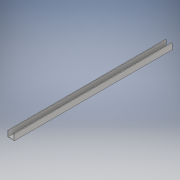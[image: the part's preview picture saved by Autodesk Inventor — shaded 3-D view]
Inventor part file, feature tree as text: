
AUTODESK INVENTOR PART (.ipt)
format: ipt  version: 2017 (Build 210142000, 142)  size: 100,864 bytes
history: native  units: in
note: dims shown in document units (in); Inventor stores cm internally (conversion verified against a paired STEP export)
features: extrude x1, sketch x1
ambient origin geometry x8: Origin, YZ Plane, XZ Plane, XY Plane, X Axis, Y Axis, Z Axis, Center Point
bodies: Solid1 (feature_tree)
feature tree (2):
  extrude  "Extrusion1"  Depth=0.0625in
  sketch  "Sketch1"  dims[d0=0.5in d2=0.0625in d3=0.0625in d4=0.0625in d5=15.0in d6=0.0in]
